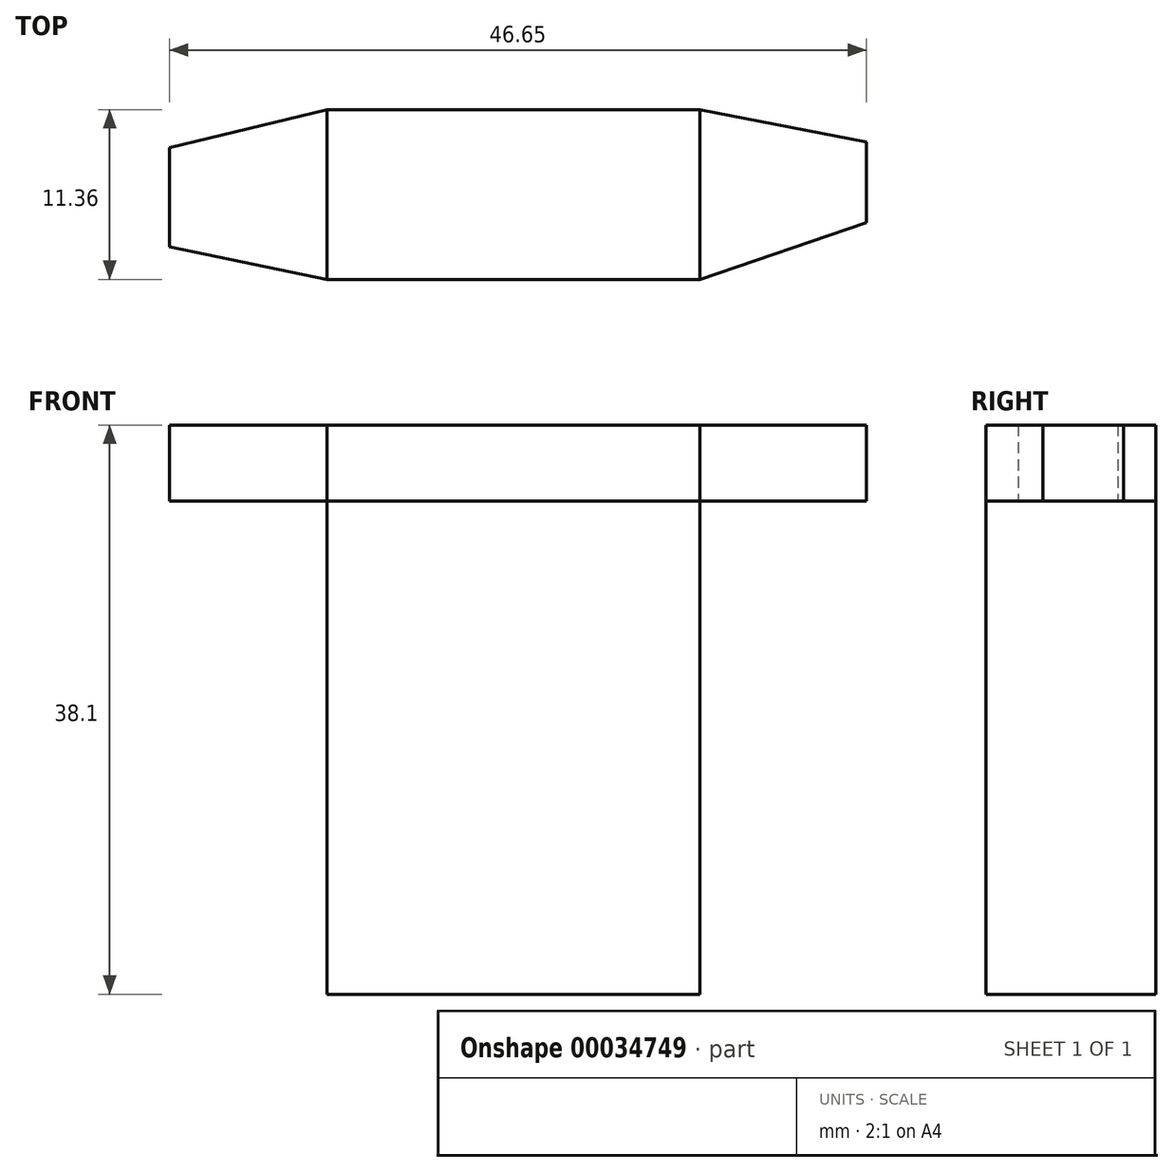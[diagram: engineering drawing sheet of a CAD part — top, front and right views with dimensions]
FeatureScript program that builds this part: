
annotation { "Feature Type Name" : "Feature", "Feature Type Description" : "" }
export const myFeature = defineFeature(function(context is Context, id is Id, definition is map)
    precondition{}
    {
        {
            var Q0;
            Q0=qCreatedBy(makeId("Top.planeOp"),FACE);
            var sketch = newSketch(context, id + "F0", { "sketchPlane" : qUnion([Q0])});
            skLineSegment(sketch, "E0.bottom", {"start": v(-12.73, 11.36) * mm, "end": v(12.23, 11.36) * mm});
            skLineSegment(sketch, "E0.top", {"start": v(-12.73, 0) * mm, "end": v(12.23, 0) * mm});
            skLineSegment(sketch, "E0.left", {"start": v(-12.73, 11.36) * mm, "end": v(-12.73, 0) * mm});
            skLineSegment(sketch, "E0.right", {"start": v(12.23, 11.36) * mm, "end": v(12.23, 0) * mm});
            skSolve(sketch);
        }
        {
            var Q0;
            Q0 = qSketchRegion(id + "F0", true);
            extrude(context, id + "F1", {"entities" : qUnion([Q0]), "depth" : 33.02 * mm});
        }
        {
            var Q0;
            Q0=makeQuery(id+"F1.opExtrude","CAP_FACE",FACE,{"disambiguationData":[OSD([sQuery(id+"F0.wireOp",EDGE,"E0.bottom"),sQuery(id+"F0.wireOp",EDGE,"E0.top"),sQuery(id+"F0.wireOp",EDGE,"E0.left"),sQuery(id+"F0.wireOp",EDGE,"E0.right")])],"isStart":false});
            var sketch = newSketch(context, id + "F2", { "sketchPlane" : qUnion([Q0])});
            skLineSegment(sketch, "E1", {"start": v(-12.73, 11.36) * mm, "end": v(-23.27, 8.82) * mm});
            skLineSegment(sketch, "E2", {"start": v(-12.73, 0) * mm, "end": v(-23.27, 2.17) * mm});
            skLineSegment(sketch, "E3", {"start": v(-23.27, 2.17) * mm, "end": v(-23.27, 8.82) * mm});
            skLineSegment(sketch, "E4", {"start": v(12.23, 11.36) * mm, "end": v(21.54, 8.82) * mm});
            skLineSegment(sketch, "E5", {"start": v(12.23, 0) * mm, "end": v(22.16, 2.11) * mm});
            skSolve(sketch);
        }
        {
            var Q0;
            Q0 = qSketchRegion(id + "F2", true);
            var Q1;
            Q1=makeQuery(id+"F2.imprint","IMPRINT",FACE,{"disambiguationData":[TD([[makeQuery(id+"F2.imprint","IMPRINT",EDGE,{"derivedFrom":sQuery(id+"F2.wireOp",EDGE,"E1")}),1.0]])]});
            extrude(context, id + "F3", {"entities" : qUnion([Q0, Q1]), "depth" : 5.08 * mm});
        }
        {
            var Q0;
            Q0=makeQuery(id+"F1.opExtrude","CAP_FACE",FACE,{"disambiguationData":[OSD([sQuery(id+"F0.wireOp",EDGE,"E0.bottom"),sQuery(id+"F0.wireOp",EDGE,"E0.top"),sQuery(id+"F0.wireOp",EDGE,"E0.left"),sQuery(id+"F0.wireOp",EDGE,"E0.right")])],"isStart":false});
            var sketch = newSketch(context, id + "F4", { "sketchPlane" : qUnion([Q0])});
            skLineSegment(sketch, "E6", {"start": v(-12.73, 11.36) * mm, "end": v(12.23, 11.36) * mm});
            skLineSegment(sketch, "E7", {"start": v(12.23, 11.36) * mm, "end": v(23.9, 9.18) * mm});
            skLineSegment(sketch, "E8", {"start": v(23.9, 9.18) * mm, "end": v(23.9, 3.02) * mm});
            skLineSegment(sketch, "E9", {"start": v(23.76, 3.02) * mm, "end": v(12.23, 0) * mm});
            skLineSegment(sketch, "E10", {"start": v(12.23, 0) * mm, "end": v(-12.73, 0) * mm});
            skLineSegment(sketch, "E11", {"start": v(-12.73, 11.36) * mm, "end": v(-12.73, 0) * mm});
            skLineSegment(sketch, "E12", {"start": v(12.23, 11.36) * mm, "end": v(12.23, 0) * mm});
            skSolve(sketch);
        }
        {
            var Q0;
            Q0 = qSketchRegion(id + "F4", true);
            extrude(context, id + "F5", {"entities" : qUnion([Q0]), "depth" : 5.08 * mm});
        }
        {
            var Q0;
            Q0=makeQuery(id+"F5.opExtrude","CAP_FACE",FACE,{"disambiguationData":[OSD([sQuery(id+"F4.wireOp",EDGE,"E6"),sQuery(id+"F4.wireOp",EDGE,"E10"),sQuery(id+"F4.wireOp",EDGE,"E11"),sQuery(id+"F4.wireOp",EDGE,"E12")])],"isStart":false});
            var sketch = newSketch(context, id + "F6", { "sketchPlane" : qUnion([Q0])});
            skLineSegment(sketch, "E13", {"start": v(12.23, 11.36) * mm, "end": v(23.38, 9.2) * mm});
            skLineSegment(sketch, "E14", {"start": v(23.38, 9.2) * mm, "end": v(23.38, 3.8) * mm});
            skLineSegment(sketch, "E15", {"start": v(23.38, 3.8) * mm, "end": v(12.23, 0) * mm});
            skSolve(sketch);
        }
        {
            var Q0;
            Q0=makeQuery(id+"F6.imprint","IMPRINT",FACE,{"disambiguationData":[TD([[makeQuery(id+"F6.imprint","IMPRINT",EDGE,{"derivedFrom":sQuery(id+"F6.wireOp",EDGE,"E13")}),-1.0]])]});
            extrude(context, id + "F7", {"entities" : qUnion([Q0]), "oppositeDirection" : true, "depth" : 5.08 * mm});
        }
    });
